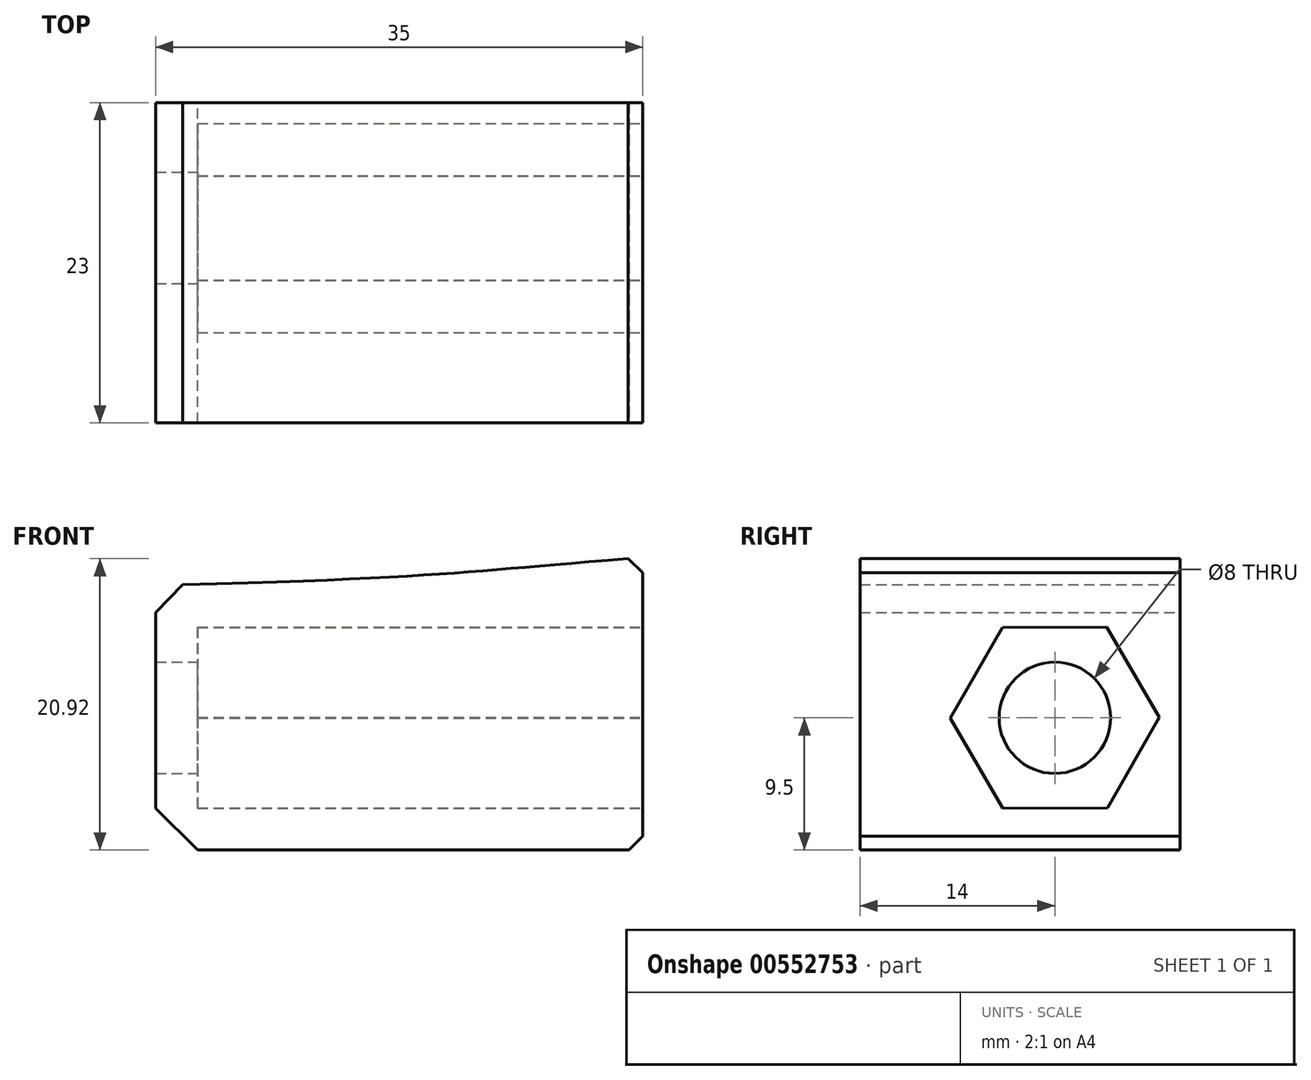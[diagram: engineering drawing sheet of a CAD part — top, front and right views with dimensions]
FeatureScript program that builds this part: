
annotation { "Feature Type Name" : "Feature", "Feature Type Description" : "" }
export const myFeature = defineFeature(function(context is Context, id is Id, definition is map)
    precondition{}
    {
        {
            var Q0;
            Q0=qCreatedBy(makeId("Front.planeOp"),FACE);
            var sketch = newSketch(context, id + "F0", { "sketchPlane" : qUnion([Q0])});
            skLineSegment(sketch, "E0", {"start": v(0, 0) * mm, "end": v(-35, 0) * mm});
            skLineSegment(sketch, "E1", {"start": v(-35, 0) * mm, "end": v(-35, 19) * mm});
            skLineSegment(sketch, "E2", {"start": v(0, 0) * mm, "end": v(0, 21) * mm});
            skFitSpline(sketch, "E3", {"points": [v(-35, 19) * mm, v(0, 21) * mm], "startDerivative": vector(66.08, 1.71) * mm, "endDerivative": vector(38.92, 2.86) * mm});
            skSolve(sketch);
        }
        {
            var Q0;
            Q0=qSketchRegion(id+"F0",true);
            extrude(context, id + "F1", {"entities" : qUnion([Q0]), "depth" : 23 * mm, "offsetDistance" : 25 * mm});
        }
        {
            var Q0;
            Q0=qCreatedBy(makeId("Right.planeOp"),FACE);
            var sketch = newSketch(context, id + "F2", { "sketchPlane" : qUnion([Q0])});
            skCircle(sketch, "E4", {"center": v(-9, 9.5) * mm, "radius": 4 * mm});
            skSolve(sketch);
        }
        {
            var Q0;
            Q0=qSketchRegion(id+"F2",true);
            extrude(context, id + "F3", {"entities" : qUnion([Q0]), "operationType" : NewBodyOperationType.REMOVE, "endBound" : BoundingType.THROUGH_ALL, "oppositeDirection" : true, "depth" : 25 * mm, "offsetDistance" : 25 * mm});
        }
        {
            var Q0;
            Q0=qCreatedBy(makeId("Right.planeOp"),FACE);
            var sketch = newSketch(context, id + "F4", { "sketchPlane" : qUnion([Q0])});
            skCircle(sketch, "E5.cCircle", {"center": v(-9, 9.5) * mm, "radius": 6.5 * mm, "construction": true});
            skLineSegment(sketch, "E5.0", {"start": v(-1.5, 9.53) * mm, "end": v(-5.23, 3.01) * mm});
            skLineSegment(sketch, "E5.1", {"start": v(-5.23, 3.01) * mm, "end": v(-12.73, 2.99) * mm});
            skLineSegment(sketch, "E5.2", {"start": v(-12.73, 2.99) * mm, "end": v(-16.5, 9.47) * mm});
            skLineSegment(sketch, "E5.3", {"start": v(-16.5, 9.47) * mm, "end": v(-12.77, 15.99) * mm});
            skLineSegment(sketch, "E5.4", {"start": v(-12.77, 15.99) * mm, "end": v(-5.27, 16.01) * mm});
            skLineSegment(sketch, "E5.5", {"start": v(-5.27, 16.01) * mm, "end": v(-1.5, 9.53) * mm});
            skPoint(sketch, "E5.0.midPoint", {"position": v(-3.36, 6.27) * mm});
            skSolve(sketch);
        }
        {
            var Q0;
            Q0=qSketchRegion(id+"F4",true);
            extrude(context, id + "F5", {"entities" : qUnion([Q0]), "operationType" : NewBodyOperationType.REMOVE, "oppositeDirection" : true, "depth" : 32 * mm, "offsetDistance" : 25 * mm});
        }
        {
            var Q0;
            Q0=makeQuery(id+"F1.opExtrude","SWEPT_EDGE",EDGE,{"disambiguationData":[OSD([sQuery(id+"F0.wireOp",EDGE,"E0"),sQuery(id+"F0.wireOp",EDGE,"E2")])]});
            chamfer(context, id + "F6", {"entities" : qUnion([Q0]), "width" : 1 * mm, "tangentPropagation" : true});
        }
        {
            var Q0;
            Q0=makeQuery(id+"F1.opExtrude","SWEPT_EDGE",EDGE,{"disambiguationData":[OSD([sQuery(id+"F0.wireOp",EDGE,"E2"),sQuery(id+"F0.wireOp",EDGE,"E3")])]});
            chamfer(context, id + "F7", {"entities" : qUnion([Q0]), "width" : 1 * mm, "tangentPropagation" : true});
        }
        {
            var Q0;
            Q0=makeQuery(id+"F1.opExtrude","SWEPT_EDGE",EDGE,{"disambiguationData":[OSD([sQuery(id+"F0.wireOp",EDGE,"E1"),sQuery(id+"F0.wireOp",EDGE,"E3")])]});
            chamfer(context, id + "F8", {"entities" : qUnion([Q0]), "width" : 2 * mm, "tangentPropagation" : true});
        }
        {
            var Q0;
            Q0=makeQuery(id+"F1.opExtrude","SWEPT_EDGE",EDGE,{"disambiguationData":[OSD([sQuery(id+"F0.wireOp",EDGE,"E0"),sQuery(id+"F0.wireOp",EDGE,"E1")])]});
            chamfer(context, id + "F9", {"entities" : qUnion([Q0]), "width" : 3 * mm, "tangentPropagation" : true});
        }
    });
